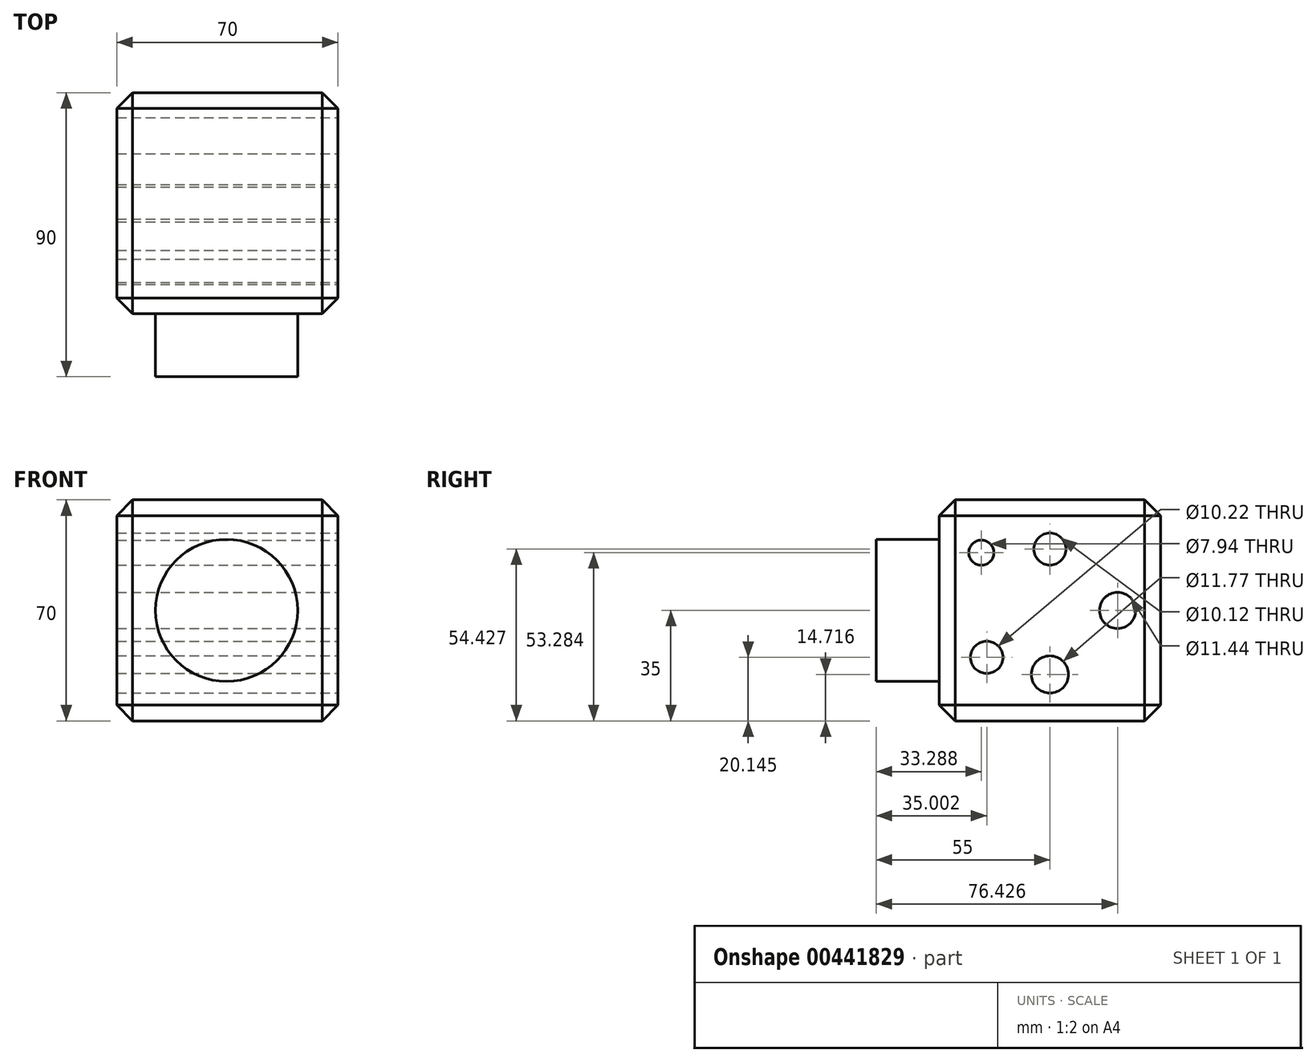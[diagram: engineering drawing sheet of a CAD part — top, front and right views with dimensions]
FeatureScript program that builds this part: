
annotation { "Feature Type Name" : "Feature", "Feature Type Description" : "" }
export const myFeature = defineFeature(function(context is Context, id is Id, definition is map)
    precondition{}
    {
        {
            var Q0;
            Q0=qCreatedBy(makeId("Top.planeOp"),FACE);
            var sketch = newSketch(context, id + "F0", { "sketchPlane" : qUnion([Q0])});
            skLineSegment(sketch, "E0.bottom", {"start": v(35, 35) * mm, "end": v(-35, 35) * mm});
            skLineSegment(sketch, "E0.top", {"start": v(35, -35) * mm, "end": v(-35, -35) * mm});
            skLineSegment(sketch, "E0.left", {"start": v(35, 35) * mm, "end": v(35, -35) * mm});
            skLineSegment(sketch, "E0.right", {"start": v(-35, 35) * mm, "end": v(-35, -35) * mm});
            skPoint(sketch, "E0.middle", {"position": v(0, 0) * mm});
            skSolve(sketch);
        }
        {
            var Q0;
            Q0=qSketchRegion(id+"F0",true);
            extrude(context, id + "F1", {"entities" : qUnion([Q0]), "endBound" : BoundingType.SYMMETRIC, "depth" : 70 * mm});
        }
        {
            var Q0;
            Q0=makeQuery(id+"F1.opExtrude","SWEPT_FACE",FACE,{"disambiguationData":[OSD([sQuery(id+"F0.wireOp",EDGE,"E0.top")])]});
            var sketch = newSketch(context, id + "F2", { "sketchPlane" : qUnion([Q0])});
            skCircle(sketch, "E1", {"center": v(-0.29, 0) * mm, "radius": 22.5 * mm});
            skSolve(sketch);
        }
        {
            var Q0;
            Q0=qSketchRegion(id+"F2",true);
            extrude(context, id + "F3", {"entities" : qUnion([Q0]), "operationType" : NewBodyOperationType.ADD, "depth" : 20 * mm});
        }
        {
            var Q0;
            Q0=makeQuery(id+"F1.opExtrude","SWEPT_FACE",FACE,{"disambiguationData":[OSD([sQuery(id+"F0.wireOp",EDGE,"E0.left")])]});
            var sketch = newSketch(context, id + "F4", { "sketchPlane" : qUnion([Q0])});
            skCircle(sketch, "E2", {"center": v(21.43, 0) * mm, "radius": 5.72 * mm});
            skCircle(sketch, "E3", {"center": v(0, 19.43) * mm, "radius": 5.06 * mm});
            skCircle(sketch, "E4", {"center": v(0, -20.28) * mm, "radius": 5.88 * mm});
            skCircle(sketch, "E5", {"center": v(-21.71, 18.28) * mm, "radius": 3.97 * mm});
            skCircle(sketch, "E6", {"center": v(-20, -14.86) * mm, "radius": 5.11 * mm});
            skSolve(sketch);
        }
        {
            var Q0;
            Q0=qSketchRegion(id+"F4",true);
            extrude(context, id + "F5", {"entities" : qUnion([Q0]), "operationType" : NewBodyOperationType.REMOVE, "oppositeDirection" : true, "depth" : 70 * mm});
        }
        {
            var Q0;
            Q0=makeQuery(id+"F1.opExtrude","CAP_EDGE",EDGE,{"disambiguationData":[OSD([sQuery(id+"F0.wireOp",EDGE,"E0.top")])],"isStart":false});
            var Q1;
            Q1=makeQuery(id+"F1.opExtrude","SWEPT_EDGE",EDGE,{"disambiguationData":[OSD([sQuery(id+"F0.wireOp",EDGE,"E0.top"),sQuery(id+"F0.wireOp",EDGE,"E0.left")])]});
            var Q2;
            Q2=makeQuery(id+"F1.opExtrude","CAP_EDGE",EDGE,{"disambiguationData":[OSD([sQuery(id+"F0.wireOp",EDGE,"E0.left")])],"isStart":false});
            var Q3;
            Q3=makeQuery(id+"F1.opExtrude","CAP_EDGE",EDGE,{"disambiguationData":[OSD([sQuery(id+"F0.wireOp",EDGE,"E0.bottom")])],"isStart":false});
            var Q4;
            Q4=makeQuery(id+"F1.opExtrude","CAP_EDGE",EDGE,{"disambiguationData":[OSD([sQuery(id+"F0.wireOp",EDGE,"E0.right")])],"isStart":false});
            var Q5;
            Q5=makeQuery(id+"F1.opExtrude","SWEPT_EDGE",EDGE,{"disambiguationData":[OSD([sQuery(id+"F0.wireOp",EDGE,"E0.bottom"),sQuery(id+"F0.wireOp",EDGE,"E0.left")])]});
            var Q6;
            Q6=makeQuery(id+"F1.opExtrude","CAP_EDGE",EDGE,{"disambiguationData":[OSD([sQuery(id+"F0.wireOp",EDGE,"E0.left")])],"isStart":true});
            var Q7;
            Q7=makeQuery(id+"F1.opExtrude","CAP_EDGE",EDGE,{"disambiguationData":[OSD([sQuery(id+"F0.wireOp",EDGE,"E0.top")])],"isStart":true});
            var Q8;
            Q8=makeQuery(id+"F1.opExtrude","SWEPT_EDGE",EDGE,{"disambiguationData":[OSD([sQuery(id+"F0.wireOp",EDGE,"E0.top"),sQuery(id+"F0.wireOp",EDGE,"E0.right")])]});
            var Q9;
            Q9=makeQuery(id+"F1.opExtrude","CAP_EDGE",EDGE,{"disambiguationData":[OSD([sQuery(id+"F0.wireOp",EDGE,"E0.bottom")])],"isStart":true});
            var Q10;
            Q10=makeQuery(id+"F1.opExtrude","CAP_EDGE",EDGE,{"disambiguationData":[OSD([sQuery(id+"F0.wireOp",EDGE,"E0.right")])],"isStart":true});
            var Q11;
            Q11=makeQuery(id+"F1.opExtrude","SWEPT_EDGE",EDGE,{"disambiguationData":[OSD([sQuery(id+"F0.wireOp",EDGE,"E0.bottom"),sQuery(id+"F0.wireOp",EDGE,"E0.right")])]});
            chamfer(context, id + "F6", {"entities" : qUnion([Q0, Q1, Q2, Q3, Q4, Q5, Q6, Q7, Q8, Q9, Q10, Q11]), "width" : 5 * mm, "tangentPropagation" : true});
        }
    });
